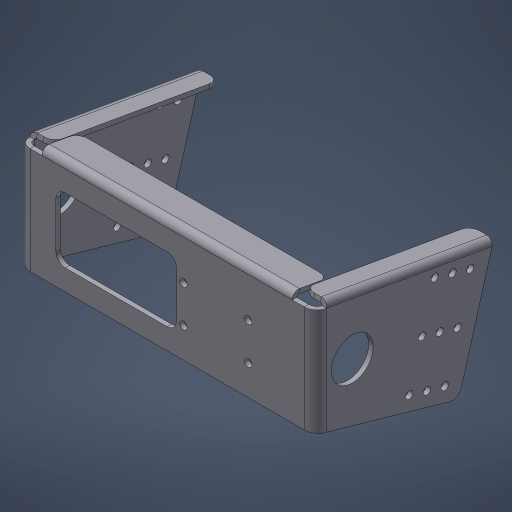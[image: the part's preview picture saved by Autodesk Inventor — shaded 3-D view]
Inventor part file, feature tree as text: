
AUTODESK INVENTOR PART (.ipt)
format: ipt  version: 2024.3 (Build 283343000, 343)  size: 522,240 bytes
history: native  units: mm (DEFAULTED — no unit token found)
features: sheet_metal_op x9, sketch x7, other x6, mirror x2, hole x2, pattern_linear x2, chamfer x1, projected_geometry x1
ambient origin geometry x8: Origin, YZ Plane, XZ Plane, XY Plane, X Axis, Y Axis, Z Axis, Center Point
bodies: Solid1 (feature_tree)
feature tree (30):
  sheet_metal_op  "Face1"
  sheet_metal_op  "Face2"
  mirror  "Mirror1"
  sheet_metal_op  "Flange2"
  sheet_metal_op  "Flange1"
  chamfer  "Corner Round1"
  hole  "Hole1"  [1 undecoded]
  pattern_linear  "Rectangular Pattern1"  Spacing1=4.572mm  [1 undecoded]
  hole  "Hole2"  [1 undecoded]
  pattern_linear  "Rectangular Pattern2"  Spacing1=1.524mm  [1 undecoded]
  mirror  "Mirror2"
  sketch  "Sketch1"  dims[d0=203.2mm d1=73.025mm]
  other  "Plate1"
  sketch  "Sketch2"  dims[d2=3.048mm]
  projected_geometry  "Projected Loop1"
  other  "Plate2"
  sheet_metal_op  "Bend1"
  sketch  "Sketch3"  dims[d5=18.50049mm]
  other  "Plate3"
  sheet_metal_op  "Bend2"
  sheet_metal_op  "Corner1"
  sketch  "Sketch4"  dims[d6=4.572mm]
  other  "Plate4"
  sheet_metal_op  "Bend3"
  sheet_metal_op  "Corner2"
  sketch  "Sketch5"  dims[d7=3.048mm]
  sketch  "Sketch6"  dims[d8=1.524mm]
  sketch  "Sketch9"  dims[d9=6.096mm d10=4.572mm d11=3.048mm d12=1.524mm d13=6.096mm d14=4.572mm d15=25.4mm d16=17.453293mm d17=1.27mm d18=12.192mm d19=3.048mm d20=4.572mm d21=3.048mm d22=1.524mm d23=6.096mm d24=4.572mm d25=15.24mm d26=90.0deg d27=1.27mm d28=12.192mm d29=3.048mm d30=4.572mm d35=6.35mm d40=99.06mm d41=13.962634mm d42=7.9375mm d43=76.2mm d44=44.45mm d45=76.2mm d46=82.55mm d47=44.45mm d48=3.048mm d49=0.0mm d50=171.45mm d52=25.4mm d53=5.1562mm d54=19.05mm d55=8.3312mm d56=5.1562mm d57=14.3117mm d58=3.048mm d59=20.594885mm d60=20.0mm d62=44.45mm d63=49.2125mm d64=28.575mm d65=22.225mm d67=9.525mm d69=25.4mm d70=4.9784mm d71=19.05mm d72=9.779mm d73=1.9558mm d74=14.3117mm d75=3.048mm d76=20.594885mm d77=30.0mm d79=31.75mm d80=25.4mm d81=1066.8mm d82=144.078655mm d83=36.175724mm d84=35.225227mm d85=15.875mm]
  other  "Cut1"
  other  "Definition1"
note: 4 required parameter values undecoded (feature->parameter linkage not recoverable at this tier; creation-order binding heuristic only, values carry confidence <= 0.55)
